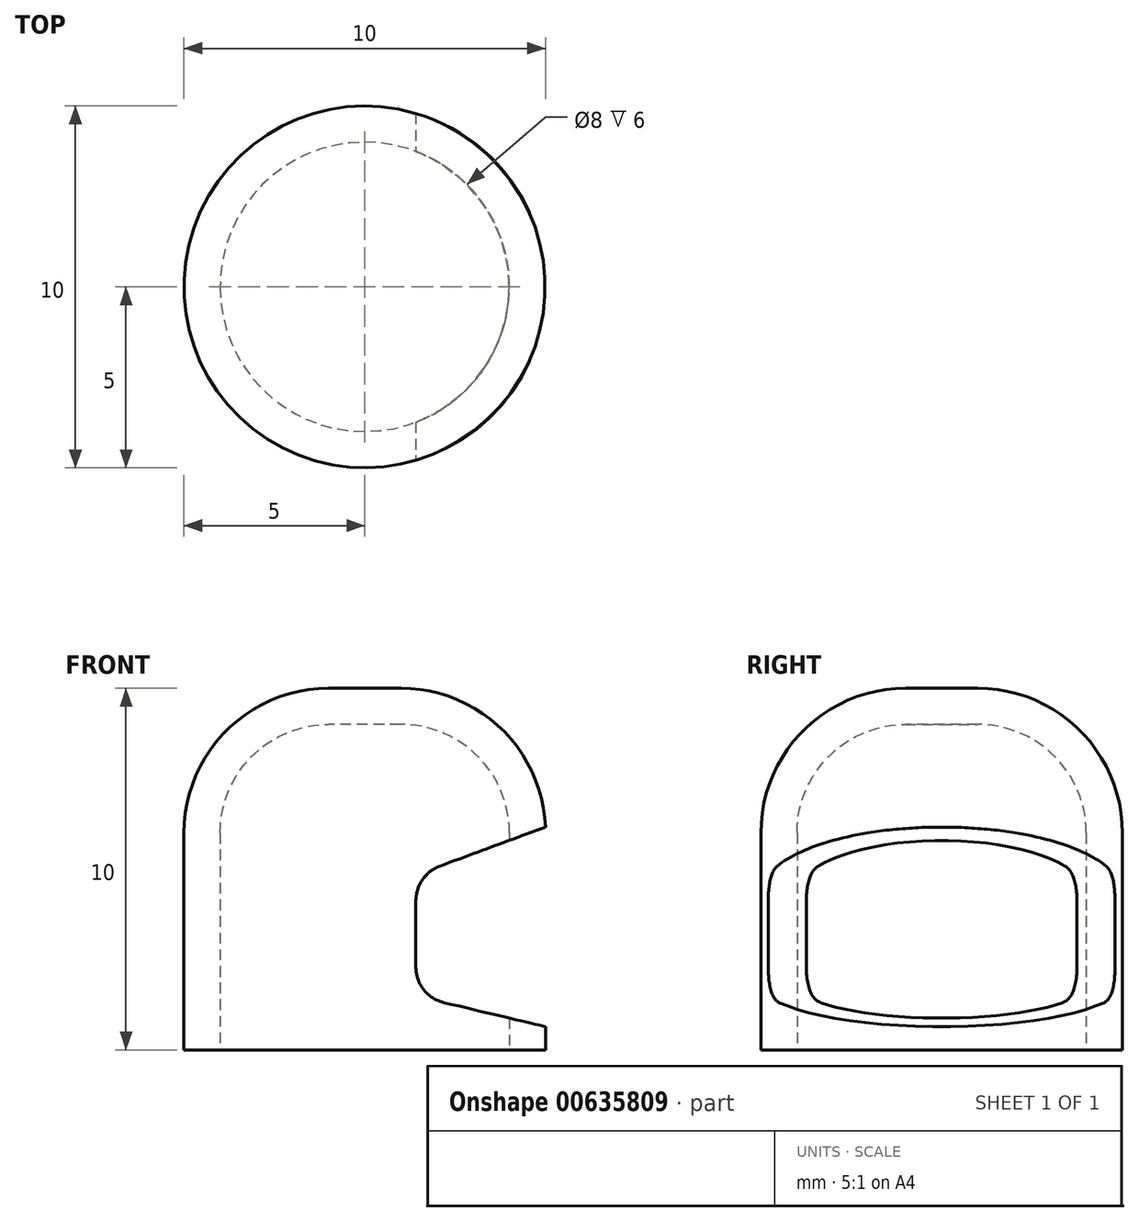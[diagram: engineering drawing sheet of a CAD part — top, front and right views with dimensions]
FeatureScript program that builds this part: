
annotation { "Feature Type Name" : "Feature", "Feature Type Description" : "" }
export const myFeature = defineFeature(function(context is Context, id is Id, definition is map)
    precondition{}
    {
        {
            var Q0;
            Q0=qCreatedBy(makeId("Top.planeOp"),FACE);
            var sketch = newSketch(context, id + "F0", { "sketchPlane" : qUnion([Q0])});
            skCircle(sketch, "E0", {"center": v(0, 0) * mm, "radius": 5 * mm});
            skSolve(sketch);
        }
        {
            var Q0;
            Q0=makeQuery(id+"F0.imprint","IMPRINT",FACE,{"disambiguationData":[TD([[makeQuery(id+"F0.imprint","IMPRINT",EDGE,{"derivedFrom":sQuery(id+"F0.wireOp",EDGE,"E0")}),1.0]])]});
            extrude(context, id + "F1", {"entities" : qUnion([Q0]), "depth" : 10 * mm, "offsetDistance" : 25.4 * mm});
        }
        {
            var Q0;
            Q0=makeQuery(id+"F1.opExtrude","CAP_EDGE",EDGE,{"disambiguationData":[OSD([sQuery(id+"F0.wireOp",EDGE,"E0")])],"isStart":false});
            fillet(context, id + "F2", {"entities" : qUnion([Q0]), "radius" : 4 * mm, "tangentPropagation" : true, "allowEdgeOverflow" : false});
        }
        {
            var Q0;
            Q0=makeQuery(id+"F1.opExtrude","CAP_FACE",FACE,{"disambiguationData":[OSD([sQuery(id+"F0.wireOp",EDGE,"E0")])],"isStart":true});
            shell(context, id + "F3", {"entities" : qUnion([Q0]), "thickness" : 1 * mm});
        }
        {
            var Q0;
            Q0=qCreatedBy(makeId("Front.planeOp"),FACE);
            var sketch = newSketch(context, id + "F4", { "sketchPlane" : qUnion([Q0])});
            skLineSegment(sketch, "E1", {"start": v(7.31, 7.02) * mm, "end": v(2.07, 5.08) * mm});
            skLineSegment(sketch, "E2", {"start": v(1.41, 4.14) * mm, "end": v(1.41, 2.28) * mm});
            skLineSegment(sketch, "E3", {"start": v(2.18, 1.3) * mm, "end": v(7.7, 0) * mm});
            skLineSegment(sketch, "E4", {"start": v(7.7, 0) * mm, "end": v(7.31, 7.02) * mm});
            skPoint(sketch, "E5.visualSharp", {"position": v(1.41, 4.84) * mm});
            skArc(sketch, "E5.filletArc", {"start": v(2.07, 5.08) * mm, "mid": v(1.6, 4.71) * mm, "end": v(1.41, 4.14) * mm});
            skPoint(sketch, "E6.visualSharp", {"position": v(1.41, 1.5) * mm});
            skArc(sketch, "E6.filletArc", {"start": v(1.41, 2.28) * mm, "mid": v(1.63, 1.66) * mm, "end": v(2.18, 1.3) * mm});
            skSolve(sketch);
        }
        {
            var Q0;
            Q0=makeQuery(id+"F4.imprint","IMPRINT",FACE,{"disambiguationData":[TD([[makeQuery(id+"F4.imprint","IMPRINT",EDGE,{"derivedFrom":sQuery(id+"F4.wireOp",EDGE,"E1")}),1.0]])]});
            extrude(context, id + "F5", {"entities" : qUnion([Q0]), "operationType" : NewBodyOperationType.REMOVE, "endBound" : BoundingType.SYMMETRIC, "oppositeDirection" : true, "depth" : 25.4 * mm, "offsetDistance" : 25.4 * mm});
        }
    });
